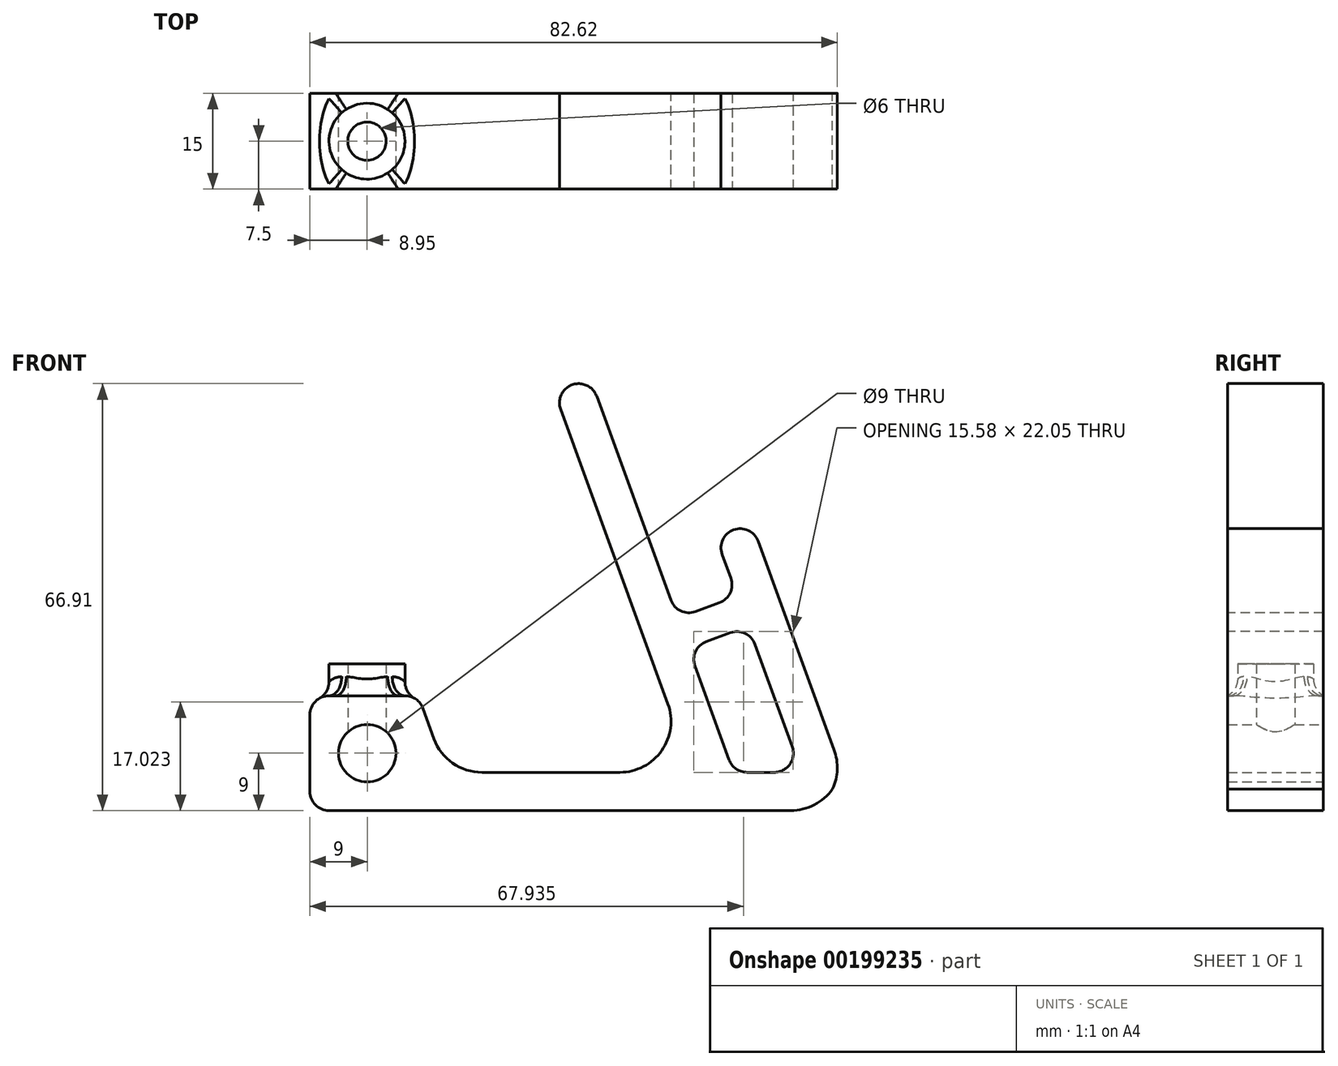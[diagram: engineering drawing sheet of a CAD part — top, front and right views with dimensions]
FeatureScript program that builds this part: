
annotation { "Feature Type Name" : "Feature", "Feature Type Description" : "" }
export const myFeature = defineFeature(function(context is Context, id is Id, definition is map)
    precondition{}
    {
        {
            var Q0;
            Q0=qCreatedBy(makeId("Front.planeOp"),FACE);
            var sketch = newSketch(context, id + "F0", { "sketchPlane" : qUnion([Q0])});
            skLineSegment(sketch, "E0", {"start": v(0, 0) * mm, "end": v(79.95, 0) * mm});
            skLineSegment(sketch, "E1", {"start": v(79.95, 0) * mm, "end": v(83.41, 6) * mm});
            skLineSegment(sketch, "E2", {"start": v(83.41, 6) * mm, "end": v(69.2, 45.04) * mm});
            skLineSegment(sketch, "E3", {"start": v(38.27, 65.7) * mm, "end": v(60, 6) * mm});
            skLineSegment(sketch, "E4", {"start": v(0, 18) * mm, "end": v(0, 0) * mm});
            skLineSegment(sketch, "E5", {"start": v(43.9, 67.76) * mm, "end": v(57.59, 30.17) * mm});
            skLineSegment(sketch, "E6", {"start": v(57.59, 30.17) * mm, "end": v(66.98, 33.6) * mm});
            skLineSegment(sketch, "E7", {"start": v(66.98, 33.6) * mm, "end": v(63.56, 42.99) * mm});
            skLineSegment(sketch, "E8.trimOffspring", {"start": v(43.9, 67.76) * mm, "end": v(38.27, 65.7) * mm});
            skLineSegment(sketch, "E9", {"start": v(63.56, 42.99) * mm, "end": v(69.2, 45.04) * mm});
            skCircle(sketch, "E10", {"center": v(9, 9) * mm, "radius": 4.5 * mm});
            skPoint(sketch, "E10.centerSnap0", {"position": v(0, 9) * mm});
            skLineSegment(sketch, "E11", {"start": v(0, 18) * mm, "end": v(17, 18) * mm});
            skLineSegment(sketch, "E12", {"start": v(17, 18) * mm, "end": v(21.37, 6) * mm});
            skLineSegment(sketch, "E13", {"start": v(21.37, 6) * mm, "end": v(60, 6) * mm});
            skLineSegment(sketch, "E14", {"start": v(57.59, 30.17) * mm, "end": v(66.39, 6) * mm, "construction": true});
            skLineSegment(sketch, "E15", {"start": v(77.03, 6) * mm, "end": v(66.98, 33.6) * mm, "construction": true});
            skLineSegment(sketch, "E16", {"start": v(66.39, 6) * mm, "end": v(59.3, 25.47) * mm});
            skLineSegment(sketch, "E17", {"start": v(59.3, 25.47) * mm, "end": v(68.7, 28.9) * mm});
            skLineSegment(sketch, "E18", {"start": v(68.7, 28.9) * mm, "end": v(77.03, 6) * mm});
            skLineSegment(sketch, "E19", {"start": v(66.39, 6) * mm, "end": v(77.03, 6) * mm});
            skLineSegment(sketch, "E20.bottom", {"start": v(13.5, 18) * mm, "end": v(4.5, 18) * mm});
            skLineSegment(sketch, "E20.top", {"start": v(13.5, 23) * mm, "end": v(4.5, 23) * mm});
            skLineSegment(sketch, "E20.left", {"start": v(13.5, 18) * mm, "end": v(13.5, 23) * mm});
            skLineSegment(sketch, "E20.right", {"start": v(4.5, 18) * mm, "end": v(4.5, 23) * mm});
            skPoint(sketch, "E20.middle", {"position": v(9, 20.5) * mm});
            skSolve(sketch);
        }
        {
            var Q0;
            Q0=makeQuery(id+"F0.imprint","IMPRINT",FACE,{"disambiguationData":[TD([[makeQuery(id+"F0.imprint","IMPRINT",EDGE,{"derivedFrom":sQuery(id+"F0.wireOp",EDGE,"E0")}),1.0]])]});
            extrude(context, id + "F1", {"entities" : qUnion([Q0]), "depth" : 15 * mm});
        }
        {
            var Q0;
            Q0=makeQuery(id+"F1.opExtrude","SWEPT_EDGE",EDGE,{"disambiguationData":[OSD([sQuery(id+"F0.wireOp",EDGE,"E3"),sQuery(id+"F0.wireOp",EDGE,"E13")])]});
            var Q1;
            Q1=makeQuery(id+"F1.opExtrude","SWEPT_EDGE",EDGE,{"disambiguationData":[OSD([sQuery(id+"F0.wireOp",EDGE,"E1"),sQuery(id+"F0.wireOp",EDGE,"E2")])]});
            var Q2;
            Q2=makeQuery(id+"F1.opExtrude","SWEPT_EDGE",EDGE,{"disambiguationData":[OSD([sQuery(id+"F0.wireOp",EDGE,"E0"),sQuery(id+"F0.wireOp",EDGE,"E1")])]});
            var Q3;
            Q3=makeQuery(id+"F1.opExtrude","SWEPT_EDGE",EDGE,{"disambiguationData":[OSD([sQuery(id+"F0.wireOp",EDGE,"E12"),sQuery(id+"F0.wireOp",EDGE,"E13")])]});
            fillet(context, id + "F2", {"entities" : qUnion([Q0, Q1, Q2, Q3]), "radius" : 8 * mm, "tangentPropagation" : true, "allowEdgeOverflow" : false});
        }
        {
            var Q0;
            Q0=makeQuery(id+"F1.opExtrude","SWEPT_EDGE",EDGE,{"disambiguationData":[OSD([sQuery(id+"F0.wireOp",EDGE,"E3"),sQuery(id+"F0.wireOp",EDGE,"E8.trimOffspring")])]});
            var Q1;
            Q1=makeQuery(id+"F1.opExtrude","SWEPT_EDGE",EDGE,{"disambiguationData":[OSD([sQuery(id+"F0.wireOp",EDGE,"E5"),sQuery(id+"F0.wireOp",EDGE,"E8.trimOffspring")])]});
            var Q2;
            Q2=makeQuery(id+"F1.opExtrude","SWEPT_EDGE",EDGE,{"disambiguationData":[OSD([sQuery(id+"F0.wireOp",EDGE,"qt00jZfL-Uh89-lZ5l-sEcP-Y7vbnNPVmedj"),sQuery(id+"F0.wireOp",EDGE,"E4")])]});
            var Q3;
            Q3=makeQuery(id+"F1.opExtrude","SWEPT_EDGE",EDGE,{"disambiguationData":[OSD([sQuery(id+"F0.wireOp",EDGE,"E0"),sQuery(id+"F0.wireOp",EDGE,"E4")])]});
            var Q4;
            Q4=makeQuery(id+"F1.opExtrude","SWEPT_EDGE",EDGE,{"disambiguationData":[OSD([sQuery(id+"F0.wireOp",EDGE,"E7"),sQuery(id+"F0.wireOp",EDGE,"E9")])]});
            var Q5;
            Q5=makeQuery(id+"F1.opExtrude","SWEPT_EDGE",EDGE,{"disambiguationData":[OSD([sQuery(id+"F0.wireOp",EDGE,"E2"),sQuery(id+"F0.wireOp",EDGE,"E9")])]});
            var Q6;
            Q6=makeQuery(id+"F1.opExtrude","SWEPT_EDGE",EDGE,{"disambiguationData":[OSD([sQuery(id+"F0.wireOp",EDGE,"E6"),sQuery(id+"F0.wireOp",EDGE,"E7")])]});
            var Q7;
            Q7=makeQuery(id+"F1.opExtrude","SWEPT_EDGE",EDGE,{"disambiguationData":[OSD([sQuery(id+"F0.wireOp",EDGE,"E5"),sQuery(id+"F0.wireOp",EDGE,"E6")])]});
            var Q8;
            Q8=makeQuery(id+"F1.opExtrude","SWEPT_EDGE",EDGE,{"disambiguationData":[OSD([sQuery(id+"F0.wireOp",EDGE,"E11"),sQuery(id+"F0.wireOp",EDGE,"E12")])]});
            var Q9;
            Q9=makeQuery(id+"F1.opExtrude","SWEPT_EDGE",EDGE,{"disambiguationData":[OSD([sQuery(id+"F0.wireOp",EDGE,"E16"),sQuery(id+"F0.wireOp",EDGE,"E17")])]});
            var Q10;
            Q10=makeQuery(id+"F1.opExtrude","SWEPT_EDGE",EDGE,{"disambiguationData":[OSD([sQuery(id+"F0.wireOp",EDGE,"2Sr4F1Lu-P07c-fWxd-7SCw-dzSF7qW4SLTE"),sQuery(id+"F0.wireOp",EDGE,"E16")])]});
            var Q11;
            Q11=makeQuery(id+"F1.opExtrude","SWEPT_EDGE",EDGE,{"disambiguationData":[OSD([sQuery(id+"F0.wireOp",EDGE,"2Sr4F1Lu-P07c-fWxd-7SCw-dzSF7qW4SLTE"),sQuery(id+"F0.wireOp",EDGE,"E18")])]});
            var Q12;
            Q12=makeQuery(id+"F1.opExtrude","SWEPT_EDGE",EDGE,{"disambiguationData":[OSD([sQuery(id+"F0.wireOp",EDGE,"E17"),sQuery(id+"F0.wireOp",EDGE,"E18")])]});
            fillet(context, id + "F3", {"entities" : qUnion([Q0, Q1, Q2, Q3, Q4, Q5, Q6, Q7, Q8, Q9, Q10, Q11, Q12]), "radius" : 3 * mm, "tangentPropagation" : true, "allowEdgeOverflow" : false});
        }
        {
            var Q0;
            Q0=makeQuery(id+"F1.opExtrude","SWEPT_FACE",FACE,{"disambiguationData":[OSD([sQuery(id+"F0.wireOp",EDGE,"E11"),sQuery(id+"F0.wireOp",EDGE,"E20.bottom")])]});
            var sketch = newSketch(context, id + "F4", { "sketchPlane" : qUnion([Q0])});
            skCircle(sketch, "E21", {"center": v(8.95, -7.5) * mm, "radius": 3 * mm});
            skPoint(sketch, "E21.centerSnap0", {"position": v(14.9, -7.5) * mm});
            skPoint(sketch, "E21.centerSnap1", {"position": v(8.95, 0) * mm});
            skCircle(sketch, "E22", {"center": v(8.95, -7.5) * mm, "radius": 5.95 * mm});
            skSolve(sketch);
        }
        {
            var Q0;
            Q0=makeQuery(id+"F4.imprint","IMPRINT",FACE,{"disambiguationData":[TD([[makeQuery(id+"F4.imprint","IMPRINT",EDGE,{"derivedFrom":sQuery(id+"F4.wireOp",EDGE,"E21")}),-1.0]])]});
            extrude(context, id + "F5", {"entities" : qUnion([Q0]), "operationType" : NewBodyOperationType.ADD, "depth" : 5 * mm});
        }
        {
            var Q0;
            Q0=makeQuery(id+"F5.boolean.opBoolean","SPLIT",FACE,{"disambiguationData":[TD([makeQuery(id+"F5.opExtrude","SWEPT_FACE",FACE,{"disambiguationData":[OSD([sQuery(id+"F4.wireOp",EDGE,"E21")])]})])],"derivedFrom":makeQuery(id+"F1.opExtrude","SWEPT_FACE",FACE,{"disambiguationData":[OSD([sQuery(id+"F0.wireOp",EDGE,"E11"),sQuery(id+"F0.wireOp",EDGE,"E20.bottom")])]})});
            extrude(context, id + "F6", {"entities" : qUnion([Q0]), "operationType" : NewBodyOperationType.REMOVE, "oppositeDirection" : true, "depth" : 10 * mm});
        }
        {
            var Q0;
            Q0=makeQuery(id+"F5.boolean.opBoolean","SPLIT",EDGE,{"disambiguationData":[OD(0.0)],"derivedFrom":makeQuery(id+"F5.opExtrude","CAP_EDGE",EDGE,{"disambiguationData":[OSD([sQuery(id+"F4.wireOp",EDGE,"E22")])],"isStart":true})});
            fillet(context, id + "F7", {"entities" : qUnion([Q0]), "radius" : 3 * mm, "tangentPropagation" : true, "allowEdgeOverflow" : false});
        }
    });
